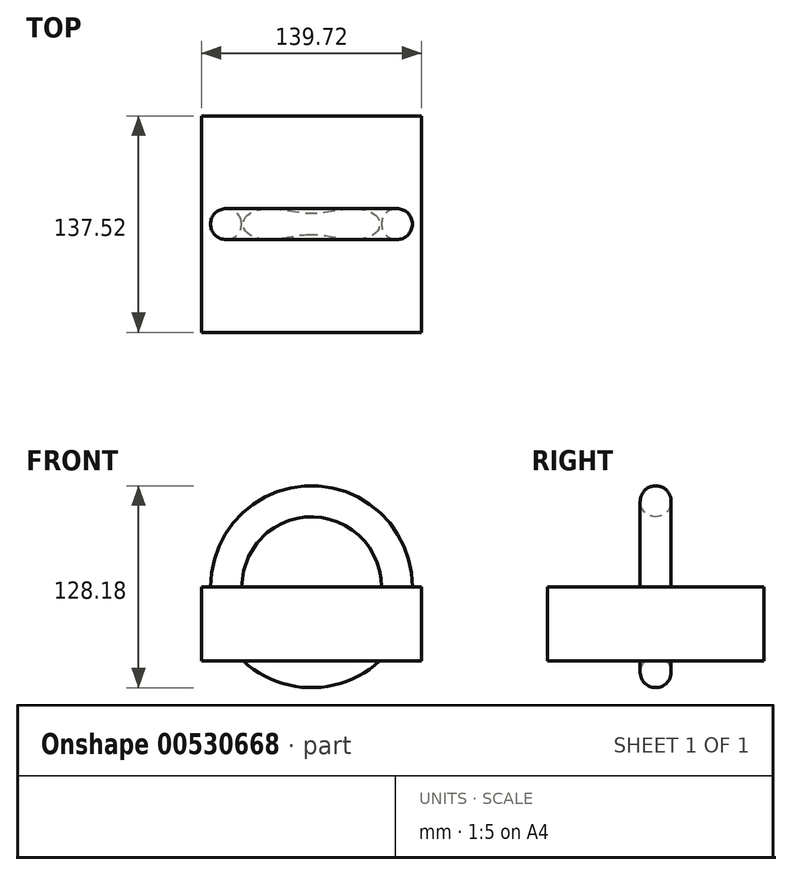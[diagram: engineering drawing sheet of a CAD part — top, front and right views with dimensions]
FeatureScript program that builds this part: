
annotation { "Feature Type Name" : "Feature", "Feature Type Description" : "" }
export const myFeature = defineFeature(function(context is Context, id is Id, definition is map)
    precondition{}
    {
        {
            var Q0;
            Q0=qCreatedBy(makeId("Top.planeOp"),FACE);
            var sketch = newSketch(context, id + "F0", { "sketchPlane" : qUnion([Q0])});
            skLineSegment(sketch, "E0.bottom", {"start": v(69.86, -68.76) * mm, "end": v(-69.86, -68.76) * mm});
            skLineSegment(sketch, "E0.top", {"start": v(69.86, 68.76) * mm, "end": v(-69.86, 68.76) * mm});
            skLineSegment(sketch, "E0.left", {"start": v(69.86, -68.76) * mm, "end": v(69.86, 68.76) * mm});
            skLineSegment(sketch, "E0.right", {"start": v(-69.86, -68.76) * mm, "end": v(-69.86, 68.76) * mm});
            skPoint(sketch, "E0.middle", {"position": v(0, 0) * mm});
            skLineSegment(sketch, "E1", {"start": v(0, 68.76) * mm, "end": v(0, -68.76) * mm});
            skSolve(sketch);
        }
        {
            var Q0;
            Q0=qCreatedBy(makeId("Top.planeOp"),FACE);
            var sketch = newSketch(context, id + "F1", { "sketchPlane" : qUnion([Q0])});
            skCircle(sketch, "E2", {"center": v(54.26, 0) * mm, "radius": 9.82 * mm});
            skSolve(sketch);
        }
        {
            var Q0;
            {var subQ0=sQuery(id+"F0.wireOp",EDGE,"E0.left");Q0=makeQuery(id+"F0.imprint","IMPRINT",FACE,{"disambiguationData":[TD([[makeQuery(id+"F0.imprint","IMPRINT",EDGE,{"derivedFrom":subQ0}),1.0]])]});}
            var Q1;
            {var subQ0=sQuery(id+"F0.wireOp",EDGE,"E0.right");Q1=makeQuery(id+"F0.imprint","IMPRINT",FACE,{"disambiguationData":[TD([[makeQuery(id+"F0.imprint","IMPRINT",EDGE,{"derivedFrom":subQ0}),-1.0]])]});}
            extrude(context, id + "F2", {"entities" : qUnion([Q0, Q1]), "oppositeDirection" : true, "depth" : 47.24 * mm, "offsetDistance" : 25.4 * mm});
        }
        {
            var Q0;
            Q0=makeQuery(id+"F1.imprint","IMPRINT",FACE,{"disambiguationData":[TD([[makeQuery(id+"F1.imprint","IMPRINT",EDGE,{"derivedFrom":sQuery(id+"F1.wireOp",EDGE,"E2")}),1.0]])]});
            var Q1;
            Q1=sQuery(id+"F0.wireOp",EDGE,"E1");
            revolve(context, id + "F3", {"operationType" : NewBodyOperationType.ADD, "entities" : qUnion([Q0]), "axis" : qUnion([Q1]), "revolveType" : RevolveType.FULL});
        }
    });
